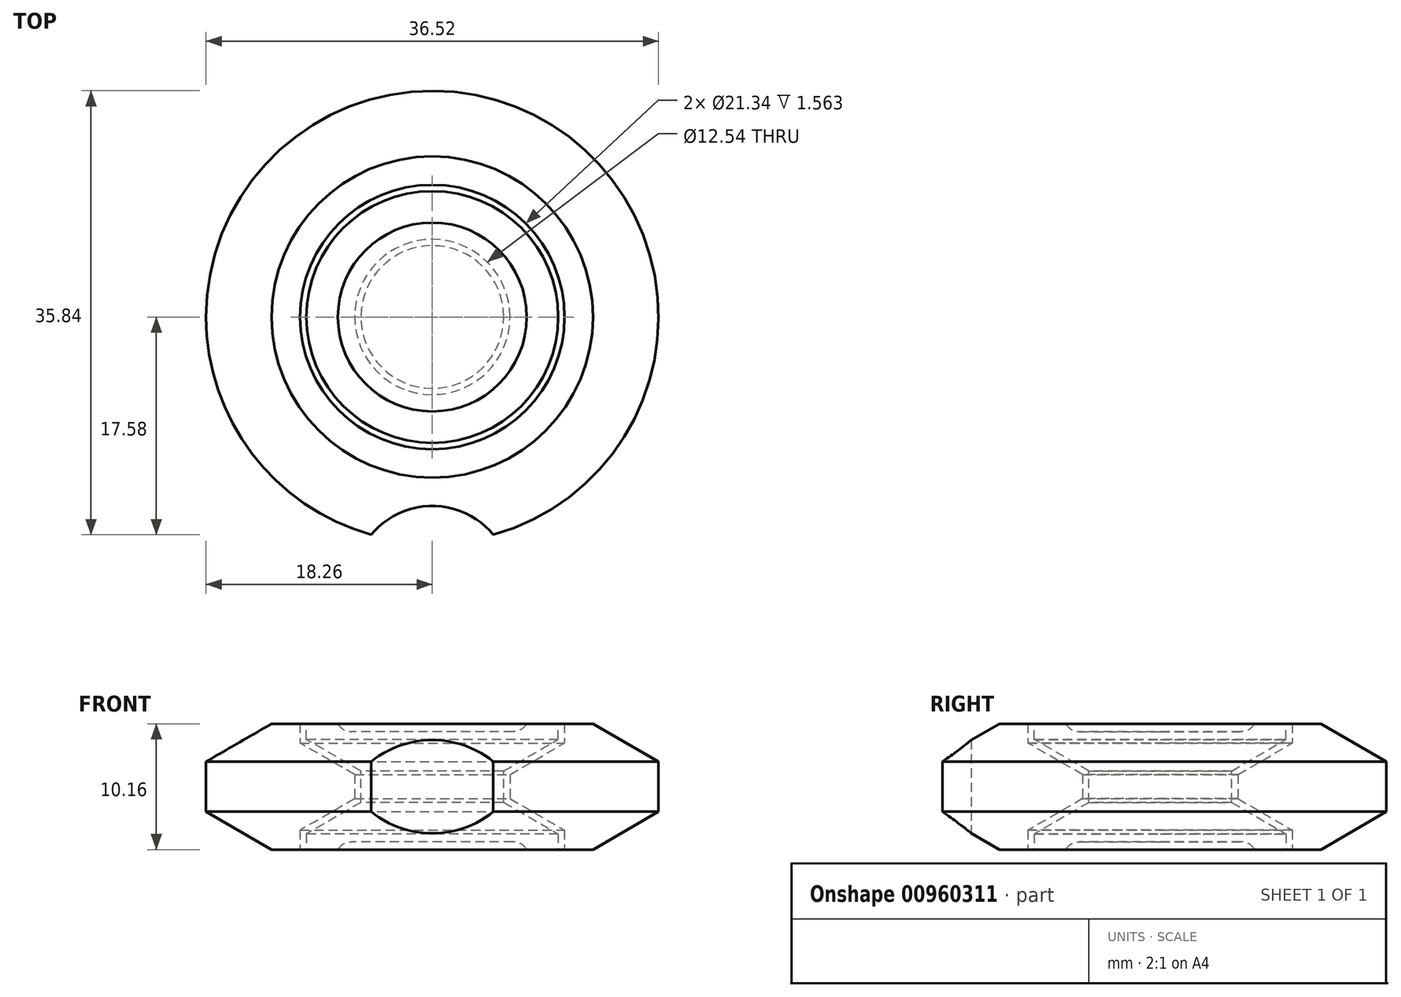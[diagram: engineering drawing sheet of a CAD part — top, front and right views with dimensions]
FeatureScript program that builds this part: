
annotation { "Feature Type Name" : "Feature", "Feature Type Description" : "" }
export const myFeature = defineFeature(function(context is Context, id is Id, definition is map)
    precondition{}
    {
        {
            var Q0;
            Q0=qCreatedBy(makeId("Front.planeOp"),FACE);
            var sketch = newSketch(context, id + "F0", { "sketchPlane" : qUnion([Q0])});
            skLineSegment(sketch, "E0", {"start": v(-5.76, 1.27) * mm, "end": v(-10.16, 3.81) * mm});
            skLineSegment(sketch, "E1", {"start": v(-10.16, 3.81) * mm, "end": v(-10.16, 5.08) * mm});
            skLineSegment(sketch, "E2", {"start": v(-10.16, 5.08) * mm, "end": v(0, 5.08) * mm});
            skLineSegment(sketch, "E3", {"start": v(-5.76, 1.27) * mm, "end": v(-5.76, 0) * mm});
            skLineSegment(sketch, "E4", {"start": v(0, 5.08) * mm, "end": v(0, 0) * mm});
            skLineSegment(sketch, "E5", {"start": v(0, 0) * mm, "end": v(-5.76, 0) * mm});
            skLineSegment(sketch, "E6.MirrorCS", {"start": v(-10.16, -3.81) * mm, "end": v(-10.16, -5.08) * mm});
            skLineSegment(sketch, "E7.MirrorCS", {"start": v(-5.76, -1.27) * mm, "end": v(-5.76, 0) * mm});
            skLineSegment(sketch, "E8.MirrorCS", {"start": v(-5.76, -1.27) * mm, "end": v(-10.16, -3.81) * mm});
            skLineSegment(sketch, "E9.MirrorCS", {"start": v(0, -5.08) * mm, "end": v(0, 0) * mm});
            skLineSegment(sketch, "E10.MirrorCS", {"start": v(-10.16, -5.08) * mm, "end": v(0, -5.08) * mm});
            skSolve(sketch);
        }
        {
            var Q0;
            Q0=makeQuery(id+"F0.imprint","IMPRINT",FACE,{"disambiguationData":[TD([[makeQuery(id+"F0.imprint","IMPRINT",EDGE,{"derivedFrom":sQuery(id+"F0.wireOp",EDGE,"E0")}),-1.0]])]});
            var Q1;
            Q1=sQuery(id+"F0.wireOp",EDGE,"E4");
            revolve(context, id + "F1", {"surfaceOperationType" : NewSurfaceOperationType.NEW, "entities" : qUnion([Q0]), "axis" : qUnion([Q1]), "revolveType" : RevolveType.FULL});
        }
        {
            var Q0;
            Q0=makeQuery(id+"F1.opRevolve","SWEPT_FACE",FACE,{"disambiguationData":[OSD([sQuery(id+"F0.wireOp",EDGE,"E2")])]});
            var sketch = newSketch(context, id + "F2", { "sketchPlane" : qUnion([Q0])});
            skCircle(sketch, "E11", {"center": v(0, 0) * mm, "radius": 7.62 * mm});
            skSolve(sketch);
        }
        {
            var Q0;
            Q0=makeQuery(id+"F2.imprint","IMPRINT",FACE,{"disambiguationData":[TD([[makeQuery(id+"F2.imprint","IMPRINT",EDGE,{"derivedFrom":sQuery(id+"F2.wireOp",EDGE,"E11")}),1.0]])]});
            extrude(context, id + "F3", {"entities" : qUnion([Q0]), "operationType" : NewBodyOperationType.REMOVE, "oppositeDirection" : true, "depth" : 0.64 * mm, "offsetDistance" : 25.4 * mm});
        }
        {
            var Q0;
            Q0=makeQuery(id+"F3.boolean.opBoolean","COPY",EDGE,{"derivedFrom":makeQuery(id+"F3.opExtrude","CAP_EDGE",EDGE,{"disambiguationData":[OSD([sQuery(id+"F2.wireOp",EDGE,"E11")])],"isStart":false})});
            fillet(context, id + "F4", {"entities" : qUnion([Q0]), "radius" : 1.27 * mm, "tangentPropagation" : true, "allowEdgeOverflow" : false});
        }
        {
            var Q0;
            Q0=makeQuery(id+"F1.opRevolve","SWEPT_BODY",BODY,{"disambiguationData":[OSD([sQuery(id+"F0.wireOp",EDGE,"E0"),sQuery(id+"F0.wireOp",EDGE,"E1"),sQuery(id+"F0.wireOp",EDGE,"E2"),sQuery(id+"F0.wireOp",EDGE,"E3"),sQuery(id+"F0.wireOp",EDGE,"E4"),sQuery(id+"F0.wireOp",EDGE,"E5")])]});
            var Q1;
            Q1=makeQuery(id+"F1.opRevolve","SWEPT_FACE",FACE,{"disambiguationData":[OSD([sQuery(id+"F0.wireOp",EDGE,"E5")])]});
            mirror(context, id + "F5", {"operationType" : NewBodyOperationType.ADD, "entities" : qUnion([Q0]), "mirrorPlane" : qUnion([Q1])});
        }
        {
            var Q0;
            Q0=qCreatedBy(makeId("Front.planeOp"),FACE);
            var sketch = newSketch(context, id + "F6", { "sketchPlane" : qUnion([Q0])});
            skLineSegment(sketch, "E12", {"start": v(0, -14.75) * mm, "end": v(0, 13.72) * mm, "construction": true});
            skLineSegment(sketch, "E13", {"start": v(-5.76, -1.27) * mm, "end": v(-5.76, 1.27) * mm, "construction": true});
            skLineSegment(sketch, "E14", {"start": v(-5.76, 1.27) * mm, "end": v(-10.16, 3.81) * mm, "construction": true});
            skLineSegment(sketch, "E15", {"start": v(-10.16, -3.81) * mm, "end": v(-5.76, -1.27) * mm, "construction": true});
            skLineSegment(sketch, "E16", {"start": v(-10.16, -5.08) * mm, "end": v(-10.16, -3.81) * mm, "construction": true});
            skLineSegment(sketch, "E17", {"start": v(-10.16, 3.81) * mm, "end": v(-10.16, 5.08) * mm, "construction": true});
            skLineSegment(sketch, "E18.0", {"start": v(-10.67, 3.52) * mm, "end": v(-10.67, 5.08) * mm});
            skLineSegment(sketch, "E18.1", {"start": v(-10.67, -5.08) * mm, "end": v(-10.67, -3.52) * mm});
            skLineSegment(sketch, "E18.2", {"start": v(-10.67, -3.52) * mm, "end": v(-6.27, -0.98) * mm});
            skLineSegment(sketch, "E18.3", {"start": v(-6.27, -0.98) * mm, "end": v(-6.27, 0.98) * mm});
            skLineSegment(sketch, "E18.4", {"start": v(-6.27, 0.98) * mm, "end": v(-10.67, 3.52) * mm});
            skLineSegment(sketch, "E19", {"start": v(-18.26, 2.02) * mm, "end": v(-18.26, -2.02) * mm});
            skLineSegment(sketch, "E20", {"start": v(-18.26, 2.02) * mm, "end": v(-12.96, 5.08) * mm});
            skLineSegment(sketch, "E21", {"start": v(-12.96, 5.08) * mm, "end": v(-10.67, 5.08) * mm});
            skLineSegment(sketch, "E22", {"start": v(-10.67, -5.08) * mm, "end": v(-12.96, -5.08) * mm});
            skLineSegment(sketch, "E23", {"start": v(-12.96, -5.08) * mm, "end": v(-18.26, -2.02) * mm});
            skSolve(sketch);
        }
        {
            var Q0;
            Q0=qSketchRegion(id+"F6",true);
            var Q1;
            Q1=sQuery(id+"F6.wireOp",EDGE,"E12");
            revolve(context, id + "F7", {"surfaceOperationType" : NewSurfaceOperationType.NEW, "entities" : qUnion([Q0]), "axis" : qUnion([Q1]), "revolveType" : RevolveType.FULL});
        }
        {
            var Q0;
            Q0=qCreatedBy(makeId("Top.planeOp"),FACE);
            var sketch = newSketch(context, id + "F8", { "sketchPlane" : qUnion([Q0])});
            skCircle(sketch, "E24", {"center": v(0, -21.59) * mm, "radius": 6.35 * mm});
            skSolve(sketch);
        }
        {
            var Q0;
            Q0=qSketchRegion(id+"F8",true);
            extrude(context, id + "F9", {"entities" : qUnion([Q0]), "operationType" : NewBodyOperationType.REMOVE, "endBound" : BoundingType.THROUGH_ALL, "depth" : 25.4 * mm, "offsetDistance" : 25.4 * mm, "hasSecondDirection" : true, "secondDirectionBound" : SecondDirectionBoundingType.THROUGH_ALL, "secondDirectionOppositeDirection" : true, "secondDirectionDepth" : 25.4 * mm});
        }
    });
